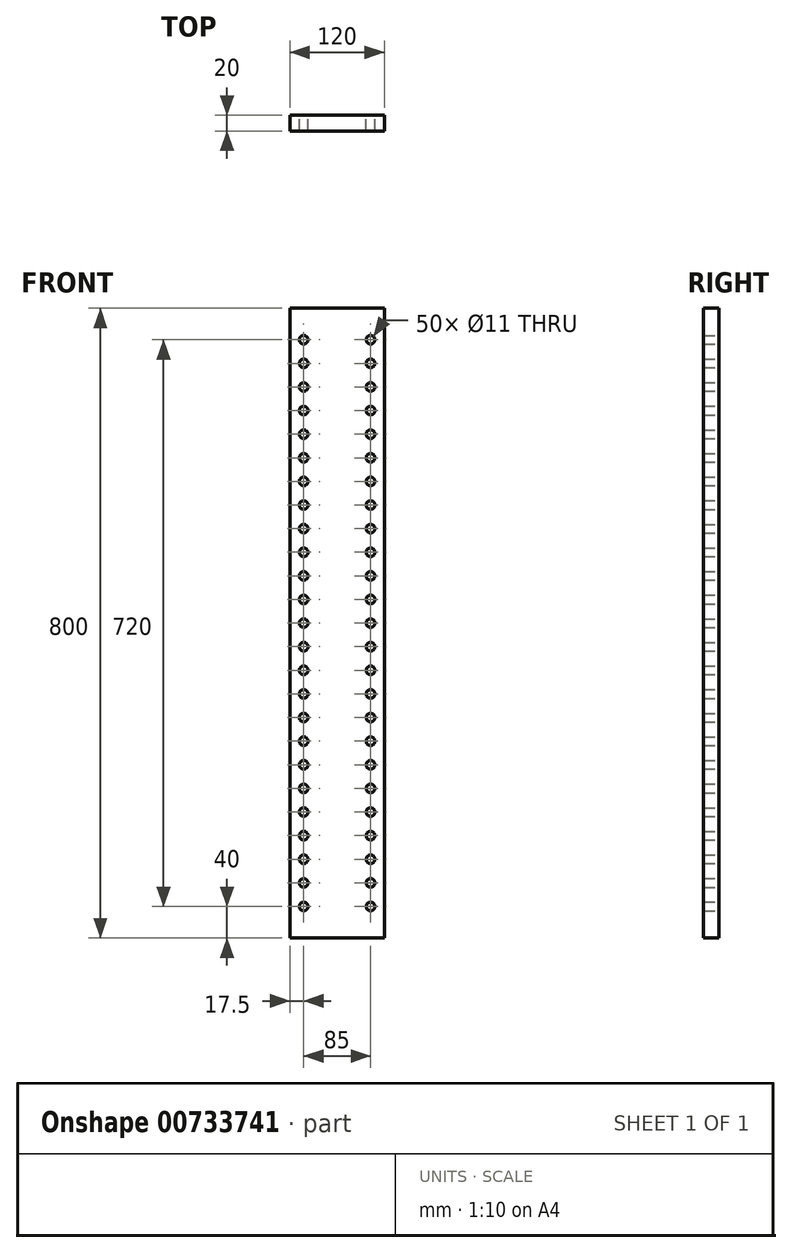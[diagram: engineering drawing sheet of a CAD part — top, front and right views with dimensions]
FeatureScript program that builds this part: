
annotation { "Feature Type Name" : "Feature", "Feature Type Description" : "" }
export const myFeature = defineFeature(function(context is Context, id is Id, definition is map)
    precondition{}
    {
        {
            var Q0;
            Q0=qCreatedBy(makeId("Front.planeOp"),FACE);
            var sketch = newSketch(context, id + "F0", { "sketchPlane" : qUnion([Q0])});
            skLineSegment(sketch, "E0.bottom", {"start": v(60, -400) * mm, "end": v(-60, -400) * mm});
            skLineSegment(sketch, "E0.top", {"start": v(60, 400) * mm, "end": v(-60, 400) * mm});
            skLineSegment(sketch, "E0.left", {"start": v(60, -400) * mm, "end": v(60, 400) * mm});
            skLineSegment(sketch, "E0.right", {"start": v(-60, -400) * mm, "end": v(-60, 400) * mm});
            skPoint(sketch, "E0.middle", {"position": v(0, 0) * mm});
            skLineSegment(sketch, "E1", {"start": v(0, 0) * mm, "end": v(-42.5, 0) * mm, "construction": true});
            skCircle(sketch, "E2", {"center": v(-42.5, 0) * mm, "radius": 5.5 * mm});
            skCircle(sketch, "E3.0.1.0", {"center": v(-42.5, 30) * mm, "radius": 5.5 * mm});
            skLineSegment(sketch, "E3.direction1", {"start": v(-42.5, 0) * mm, "end": v(-17.5, 0) * mm, "construction": true});
            skLineSegment(sketch, "E3.direction2", {"start": v(-42.5, 0) * mm, "end": v(-42.5, 30) * mm, "construction": true});
            skCircle(sketch, "E4.0.0.2", {"center": v(-42.5, 60) * mm, "radius": 5.5 * mm});
            skCircle(sketch, "E4.0.0.3", {"center": v(-42.5, 90) * mm, "radius": 5.5 * mm});
            skCircle(sketch, "E4.0.0.4", {"center": v(-42.5, 120) * mm, "radius": 5.5 * mm});
            skCircle(sketch, "E4.0.0.5", {"center": v(-42.5, 150) * mm, "radius": 5.5 * mm});
            skCircle(sketch, "E4.0.0.6", {"center": v(-42.5, 180) * mm, "radius": 5.5 * mm});
            skCircle(sketch, "E4.0.0.7", {"center": v(-42.5, 210) * mm, "radius": 5.5 * mm});
            skCircle(sketch, "E4.0.0.8", {"center": v(-42.5, 240) * mm, "radius": 5.5 * mm});
            skCircle(sketch, "E5.0.0.9", {"center": v(-42.5, 270) * mm, "radius": 5.5 * mm});
            skLineSegment(sketch, "E6", {"start": v(0, 0) * mm, "end": v(0, 100) * mm, "construction": true});
            skCircle(sketch, "E7.MirrorC", {"center": v(42.5, 0) * mm, "radius": 5.5 * mm});
            skCircle(sketch, "E8.MirrorC", {"center": v(42.5, 30) * mm, "radius": 5.5 * mm});
            skCircle(sketch, "E9.MirrorC", {"center": v(42.5, 60) * mm, "radius": 5.5 * mm});
            skCircle(sketch, "E10.MirrorC", {"center": v(42.5, 90) * mm, "radius": 5.5 * mm});
            skCircle(sketch, "E11.MirrorC", {"center": v(42.5, 270) * mm, "radius": 5.5 * mm});
            skCircle(sketch, "E12.MirrorC", {"center": v(42.5, 240) * mm, "radius": 5.5 * mm});
            skCircle(sketch, "E13.MirrorC", {"center": v(42.5, 210) * mm, "radius": 5.5 * mm});
            skCircle(sketch, "E14.MirrorC", {"center": v(42.5, 180) * mm, "radius": 5.5 * mm});
            skCircle(sketch, "E15.MirrorC", {"center": v(42.5, 150) * mm, "radius": 5.5 * mm});
            skCircle(sketch, "E16.MirrorC", {"center": v(42.5, 120) * mm, "radius": 5.5 * mm});
            skCircle(sketch, "E17.MirrorC", {"center": v(-42.5, -30) * mm, "radius": 5.5 * mm});
            skCircle(sketch, "E18.MirrorC", {"center": v(42.5, -180) * mm, "radius": 5.5 * mm});
            skCircle(sketch, "E19.MirrorC", {"center": v(42.5, -270) * mm, "radius": 5.5 * mm});
            skCircle(sketch, "E20.MirrorC", {"center": v(-42.5, -60) * mm, "radius": 5.5 * mm});
            skCircle(sketch, "E21.MirrorC", {"center": v(-42.5, -270) * mm, "radius": 5.5 * mm});
            skCircle(sketch, "E22.MirrorC", {"center": v(42.5, -60) * mm, "radius": 5.5 * mm});
            skCircle(sketch, "E23.MirrorC", {"center": v(42.5, -240) * mm, "radius": 5.5 * mm});
            skCircle(sketch, "E24.MirrorC", {"center": v(42.5, -120) * mm, "radius": 5.5 * mm});
            skCircle(sketch, "E25.MirrorC", {"center": v(42.5, -210) * mm, "radius": 5.5 * mm});
            skCircle(sketch, "E26.MirrorC", {"center": v(-42.5, -180) * mm, "radius": 5.5 * mm});
            skCircle(sketch, "E27.MirrorC", {"center": v(-42.5, -210) * mm, "radius": 5.5 * mm});
            skCircle(sketch, "E28.MirrorC", {"center": v(42.5, -30) * mm, "radius": 5.5 * mm});
            skCircle(sketch, "E29.MirrorC", {"center": v(42.5, -150) * mm, "radius": 5.5 * mm});
            skCircle(sketch, "E30.MirrorC", {"center": v(42.5, -90) * mm, "radius": 5.5 * mm});
            skCircle(sketch, "E31.MirrorC", {"center": v(-42.5, -150) * mm, "radius": 5.5 * mm});
            skCircle(sketch, "E32.MirrorC", {"center": v(-42.5, -120) * mm, "radius": 5.5 * mm});
            skCircle(sketch, "E33.MirrorC", {"center": v(-42.5, -90) * mm, "radius": 5.5 * mm});
            skCircle(sketch, "E34.MirrorC", {"center": v(-42.5, -240) * mm, "radius": 5.5 * mm});
            skLineSegment(sketch, "E35.MirrorCS", {"start": v(-42.5, 0) * mm, "end": v(-42.5, -30) * mm, "construction": true});
            skLineSegment(sketch, "E36.MirrorCS", {"start": v(0, 0) * mm, "end": v(0, -100) * mm, "construction": true});
            skCircle(sketch, "E37.0.0.10", {"center": v(-42.5, 300) * mm, "radius": 5.5 * mm});
            skCircle(sketch, "E37.0.0.11", {"center": v(-42.5, 330) * mm, "radius": 5.5 * mm});
            skCircle(sketch, "E37.0.0.12", {"center": v(-42.5, 360) * mm, "radius": 5.5 * mm});
            skCircle(sketch, "E38.MirrorC", {"center": v(42.5, 300) * mm, "radius": 5.5 * mm});
            skCircle(sketch, "E39.MirrorC", {"center": v(42.5, 330) * mm, "radius": 5.5 * mm});
            skCircle(sketch, "E40.MirrorC", {"center": v(42.5, 360) * mm, "radius": 5.5 * mm});
            skCircle(sketch, "E41.MirrorC", {"center": v(42.5, -300) * mm, "radius": 5.5 * mm});
            skCircle(sketch, "E42.MirrorC", {"center": v(42.5, -330) * mm, "radius": 5.5 * mm});
            skCircle(sketch, "E43.MirrorC", {"center": v(42.5, -360) * mm, "radius": 5.5 * mm});
            skCircle(sketch, "E44.MirrorC", {"center": v(-42.5, -330) * mm, "radius": 5.5 * mm});
            skCircle(sketch, "E45.MirrorC", {"center": v(-42.5, -300) * mm, "radius": 5.5 * mm});
            skCircle(sketch, "E46.MirrorC", {"center": v(-42.5, -360) * mm, "radius": 5.5 * mm});
            skSolve(sketch);
        }
        {
            var Q0;
            Q0=qSketchRegion(id+"F0",true);
            extrude(context, id + "F1", {"entities" : qUnion([Q0]), "depth" : 20 * mm, "offsetDistance" : 25 * mm});
        }
    });
